# Revit family: Silla Petrus
name_source: partatom
category: Furniture
units: mm (PartAtom-declared; Revit-internal decimal feet)

## family parameters
Always vertical = Yes
Cut with Voids When Loaded = No
OmniClass Number = 23.40.20.00
OmniClass Title = General Furniture and Specialties
Room Calculation Point = No
Shared = No
Work Plane-Based = No

## types (2) — shared parameters
A = 0.6 m
Fabricante = BENITO URBAN SL
Ficha_Tecnica = https://www.benito.com
Material = Hormigón prefabricado
Silla Petrus-UM359-1640mm = No
Silla Petrus-UM359T-600mm = No
URL_Producto = https://www.benito.com
zero-valued in all types: Default Elevation

## per-type parameters (varying)
| type | B | Description | H | H1 | Referencia | Type Comments |
| Silla Petrus-UM359S-600mm | 0.6 m | Banco fabricado en hormigón prefabricado color gris granítico de aspecto rugoso. Se puede colocar en elementos aislados o en grupos. | 0.47 m | 0 m | UM359S | Anclaje recomendado: Apoyado por su propio peso. |
| Silla Petrus-UM359SR-600mm | 0.8 m | Banco fabricado en hormigón prefabricado color gris granítico de aspecto rugoso. Se puede colocar en elementos aislados o en grupos | 0.82 m | 0.46 m | UM359SR | Anclaje recomendado: Apoyado por su propio peso |

type visibility flags: 2 boolean params named "<type name>" — each type sets only its own to Yes (folded from table)

## geometry (parser evidence)
native form markers: Blend x4, Sweep x14
no freeform markers — native parametric forms only
